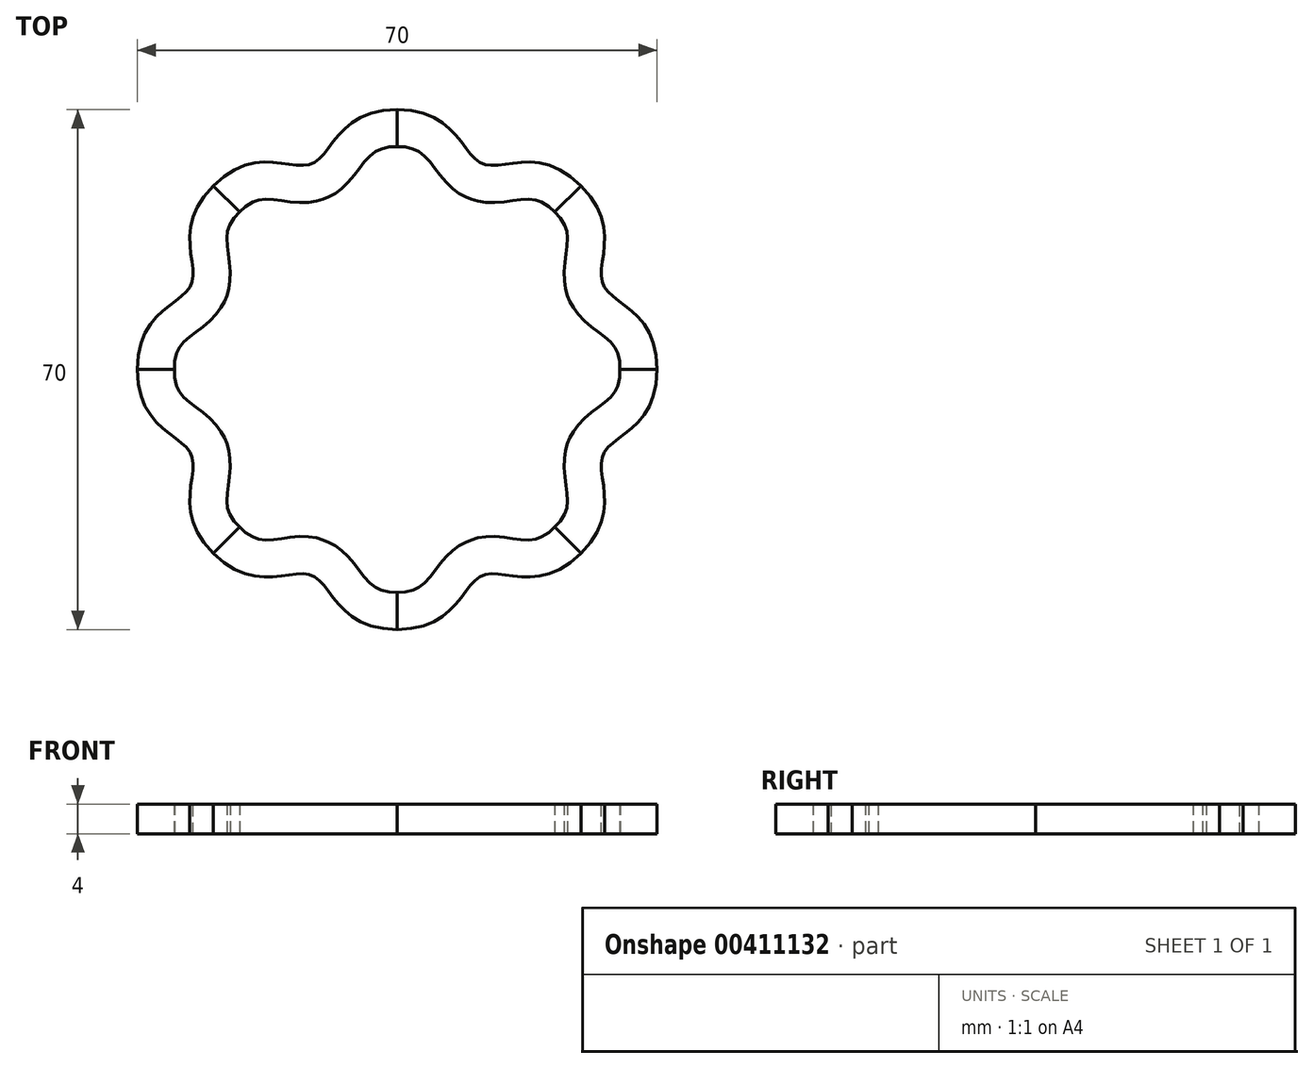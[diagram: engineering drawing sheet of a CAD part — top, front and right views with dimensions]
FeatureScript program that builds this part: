
annotation { "Feature Type Name" : "Feature", "Feature Type Description" : "" }
export const myFeature = defineFeature(function(context is Context, id is Id, definition is map)
    precondition{}
    {
        {
            var Q0;
            Q0=qCreatedBy(makeId("Top.planeOp"),FACE);
            var sketch = newSketch(context, id + "F0", { "sketchPlane" : qUnion([Q0])});
            skLineSegment(sketch, "E0", {"start": v(0, 0) * mm, "end": v(13.4, 32.34) * mm, "construction": true});
            skLineSegment(sketch, "E1", {"start": v(-15.7, 35) * mm, "end": v(11.65, 35) * mm, "construction": true});
            skLineSegment(sketch, "E2", {"start": v(24.75, 24.75) * mm, "end": v(13.44, 36.06) * mm, "construction": true});
            skFitSpline(sketch, "E3", {"points": [v(0, 35) * mm, v(11.48, 27.72) * mm, v(24.75, 24.75) * mm], "startDerivative": vector(48, 0) * mm, "endDerivative": vector(33.94, -33.94) * mm});
            skFitSpline(sketch, "E4.0", {"points": [v(0, 30) * mm, v(0.68, 30) * mm, v(1.47, 29.9) * mm, v(2.2, 29.7) * mm, v(2.63, 29.52) * mm, v(2.99, 29.32) * mm, v(3.43, 29) * mm, v(3.87, 28.58) * mm, v(4.36, 28.01) * mm, v(4.76, 27.5) * mm, v(5.2, 26.92) * mm, v(5.7, 26.26) * mm, v(6.3, 25.51) * mm, v(6.95, 24.83) * mm, v(7.6, 24.27) * mm, v(8.16, 23.84) * mm, v(8.7, 23.51) * mm, v(9.18, 23.26) * mm, v(9.57, 23.1) * mm, v(9.96, 22.94) * mm, v(10.47, 22.78) * mm, v(11.09, 22.63) * mm, v(11.78, 22.53) * mm, v(12.64, 22.47) * mm, v(13.58, 22.5) * mm, v(14.54, 22.6) * mm, v(15.36, 22.7) * mm, v(16.08, 22.81) * mm, v(16.72, 22.9) * mm, v(17.47, 22.95) * mm, v(18.08, 22.93) * mm, v(18.62, 22.84) * mm, v(19.02, 22.73) * mm, v(19.45, 22.55) * mm, v(20.1, 22.19) * mm, v(20.73, 21.7) * mm, v(21.21, 21.21) * mm]});
            skLineSegment(sketch, "E5", {"start": v(0, 30) * mm, "end": v(0, 35) * mm});
            skLineSegment(sketch, "E6", {"start": v(21.21, 21.21) * mm, "end": v(24.75, 24.75) * mm});
            skSolve(sketch);
        }
        {
            var Q0;
            Q0=qSketchRegion(id+"F0",true);
            extrude(context, id + "F1", {"entities" : qUnion([Q0]), "depth" : 4 * mm});
        }
        {
            var Q0;
            Q0=qCreatedBy(makeId("Front.planeOp"),FACE);
            var sketch = newSketch(context, id + "F2", { "sketchPlane" : qUnion([Q0])});
            skLineSegment(sketch, "E7", {"start": v(0, 0) * mm, "end": v(0, 46.86) * mm});
            skSolve(sketch);
        }
        {
            var Q0;
            Q0=makeQuery(id+"F1.opExtrude","SWEPT_BODY",BODY,{"disambiguationData":[OSD([sQuery(id+"F0.wireOp",EDGE,"E3"),sQuery(id+"F0.wireOp",EDGE,"E4.0"),sQuery(id+"F0.wireOp",EDGE,"E5"),sQuery(id+"F0.wireOp",EDGE,"E6")])]});
            var Q1;
            Q1=sQuery(id+"F2.wireOp",EDGE,"E7");
            circularPattern(context, id + "F3", {"entities" : qUnion([Q0]), "axis" : qUnion([Q1]), "angle" : 360 * degree, "instanceCount" : 8, "equalSpace" : true});
        }
    });
